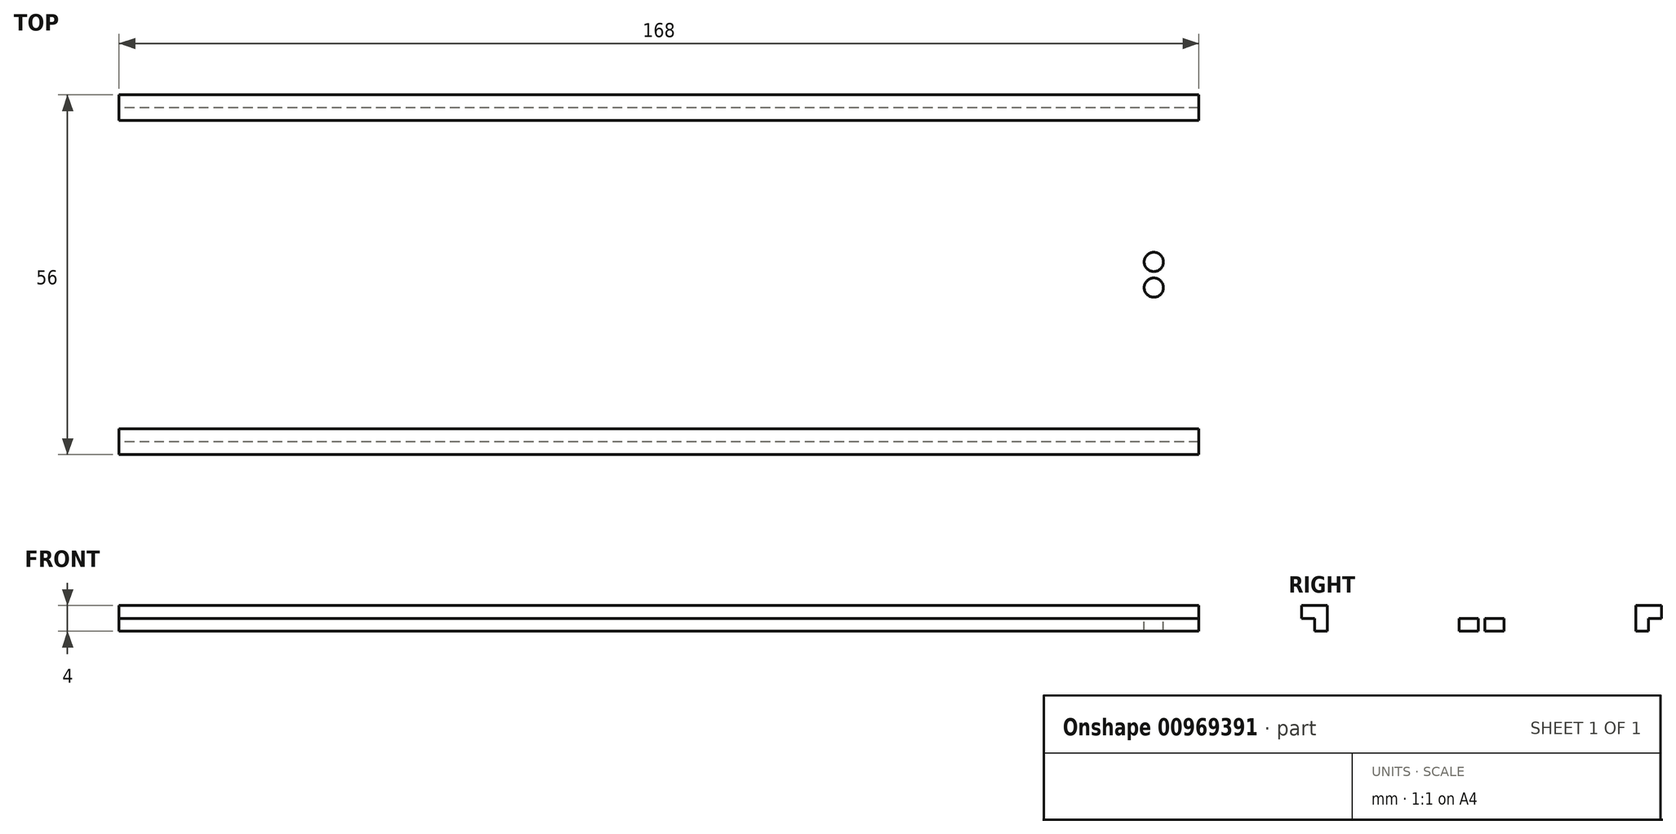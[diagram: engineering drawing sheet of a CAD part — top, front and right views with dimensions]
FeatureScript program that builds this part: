
annotation { "Feature Type Name" : "Feature", "Feature Type Description" : "" }
export const myFeature = defineFeature(function(context is Context, id is Id, definition is map)
    precondition{}
    {
        {
            var Q0;
            Q0=qCreatedBy(makeId("Top.planeOp"),FACE);
            var sketch = newSketch(context, id + "F0", { "sketchPlane" : qUnion([Q0])});
            skLineSegment(sketch, "E0.bottom", {"start": v(84, -26) * mm, "end": v(-84, -26) * mm});
            skLineSegment(sketch, "E0.top", {"start": v(84, 26) * mm, "end": v(-84, 26) * mm});
            skLineSegment(sketch, "E0.left", {"start": v(84, -26) * mm, "end": v(84, 26) * mm});
            skLineSegment(sketch, "E0.right", {"start": v(-84, -26) * mm, "end": v(-84, 26) * mm});
            skPoint(sketch, "E0.middle", {"position": v(0, 0) * mm});
            skSolve(sketch);
        }
        {
            var Q0;
            Q0=makeQuery(id+"F0.imprint","IMPRINT",FACE,{"disambiguationData":[TD([[makeQuery(id+"F0.imprint","IMPRINT",EDGE,{"derivedFrom":sQuery(id+"F0.wireOp",EDGE,"E0.bottom")}),-1.0]])]});
            extrude(context, id + "F1", {"entities" : qUnion([Q0]), "depth" : 2 * mm, "offsetDistance" : 25 * mm});
        }
        {
            var Q0;
            Q0=makeQuery(id+"F1.opExtrude","CAP_FACE",FACE,{"disambiguationData":[OSD([sQuery(id+"F0.wireOp",EDGE,"E0.bottom"),sQuery(id+"F0.wireOp",EDGE,"E0.top"),sQuery(id+"F0.wireOp",EDGE,"E0.left"),sQuery(id+"F0.wireOp",EDGE,"E0.right")])],"isStart":false});
            var sketch = newSketch(context, id + "F2", { "sketchPlane" : qUnion([Q0])});
            skLineSegment(sketch, "E1.bottom", {"start": v(-84, -24) * mm, "end": v(84, -24) * mm});
            skLineSegment(sketch, "E1.top", {"start": v(-84, -28) * mm, "end": v(84, -28) * mm});
            skLineSegment(sketch, "E1.left", {"start": v(-84, -24) * mm, "end": v(-84, -28) * mm});
            skLineSegment(sketch, "E1.right", {"start": v(84, -24) * mm, "end": v(84, -28) * mm});
            skLineSegment(sketch, "E2.bottom", {"start": v(-84, 24) * mm, "end": v(84, 24) * mm});
            skLineSegment(sketch, "E2.top", {"start": v(-84, 28) * mm, "end": v(84, 28) * mm});
            skLineSegment(sketch, "E2.left", {"start": v(-84, 24) * mm, "end": v(-84, 28) * mm});
            skLineSegment(sketch, "E2.right", {"start": v(84, 24) * mm, "end": v(84, 28) * mm});
            skSolve(sketch);
        }
        {
            var Q0;
            {var subQ0=sQuery(id+"F2.wireOp",EDGE,"E1.top");Q0=makeQuery(id+"F2.imprint","IMPRINT",FACE,{"disambiguationData":[TD([[makeQuery(id+"F2.imprint","IMPRINT",EDGE,{"derivedFrom":subQ0}),1.0]])]});}
            var Q1;
            {var subQ0=sQuery(id+"F2.wireOp",EDGE,"E1.bottom");Q1=makeQuery(id+"F2.imprint","IMPRINT",FACE,{"disambiguationData":[TD([[makeQuery(id+"F2.imprint","IMPRINT",EDGE,{"derivedFrom":subQ0}),-1.0]])]});}
            var Q2;
            {var subQ0=sQuery(id+"F2.wireOp",EDGE,"E2.bottom");Q2=makeQuery(id+"F2.imprint","IMPRINT",FACE,{"disambiguationData":[TD([[makeQuery(id+"F2.imprint","IMPRINT",EDGE,{"derivedFrom":subQ0}),1.0]])]});}
            var Q3;
            {var subQ0=sQuery(id+"F2.wireOp",EDGE,"E2.top");Q3=makeQuery(id+"F2.imprint","IMPRINT",FACE,{"disambiguationData":[TD([[makeQuery(id+"F2.imprint","IMPRINT",EDGE,{"derivedFrom":subQ0}),-1.0]])]});}
            extrude(context, id + "F3", {"entities" : qUnion([Q0, Q1, Q2, Q3]), "operationType" : NewBodyOperationType.ADD, "depth" : 2 * mm, "offsetDistance" : 25 * mm});
        }
        {
            var Q0;
            Q0=makeQuery(id+"F1.opExtrude","CAP_FACE",FACE,{"disambiguationData":[OSD([sQuery(id+"F0.wireOp",EDGE,"E0.bottom"),sQuery(id+"F0.wireOp",EDGE,"E0.top"),sQuery(id+"F0.wireOp",EDGE,"E0.left"),sQuery(id+"F0.wireOp",EDGE,"E0.right")])],"isStart":false});
            var sketch = newSketch(context, id + "F4", { "sketchPlane" : qUnion([Q0])});
            skLineSegment(sketch, "E3", {"start": v(-84, 0) * mm, "end": v(84, 0) * mm, "construction": true});
            skPoint(sketch, "E4", {"position": v(-77, 0) * mm});
            skLineSegment(sketch, "E5", {"start": v(-77, 0) * mm, "end": v(-77, 2) * mm, "construction": true});
            skLineSegment(sketch, "E6", {"start": v(-77, 0) * mm, "end": v(-77, -2) * mm, "construction": true});
            skCircle(sketch, "E7", {"center": v(-77, -2) * mm, "radius": 1.5 * mm});
            skCircle(sketch, "E8", {"center": v(-77, 2) * mm, "radius": 1.5 * mm});
            skLineSegment(sketch, "E9", {"start": v(-76, 0.88) * mm, "end": v(-76, -0.88) * mm});
            skLineSegment(sketch, "E10", {"start": v(-78, 0.88) * mm, "end": v(-78, -0.88) * mm});
            skLineSegment(sketch, "E11", {"start": v(0, 24) * mm, "end": v(0, -24) * mm, "construction": true});
            skLineSegment(sketch, "E12.MirrorCS", {"start": v(77, 0) * mm, "end": v(77, -2) * mm, "construction": true});
            skPoint(sketch, "E13.MirrorP", {"position": v(77, 0) * mm});
            skLineSegment(sketch, "E14.MirrorCS", {"start": v(78, 0.88) * mm, "end": v(78, -0.88) * mm});
            skLineSegment(sketch, "E15.MirrorCS", {"start": v(84, 0) * mm, "end": v(-84, 0) * mm, "construction": true});
            skLineSegment(sketch, "E16.MirrorCS", {"start": v(77, 0) * mm, "end": v(77, 2) * mm, "construction": true});
            skLineSegment(sketch, "E17.MirrorCS", {"start": v(76, 0.88) * mm, "end": v(76, -0.88) * mm});
            skCircle(sketch, "E18.MirrorC", {"center": v(77, -2) * mm, "radius": 1.5 * mm});
            skCircle(sketch, "E19.MirrorC", {"center": v(77, 2) * mm, "radius": 1.5 * mm});
            skSolve(sketch);
        }
        {
            var Q0;
            {var subQ0=sQuery(id+"F4.wireOp",EDGE,"E18.MirrorC");var subQ1=makeQuery(id+"F4.imprint","INTERSECT",VERTEX,{"derivedFrom":[sQuery(id+"F4.wireOp",EDGE,"E14.MirrorCS"),subQ0]});Q0=makeQuery(id+"F4.imprint","IMPRINT",FACE,{"disambiguationData":[TD([[makeQuery(id+"F4.imprint","IMPRINT",EDGE,{"disambiguationData":[TD([[subQ1,1.0]])],"derivedFrom":subQ0}),-1.0]])]});}
            var Q1;
            {var subQ0=sQuery(id+"F4.wireOp",EDGE,"E14.MirrorCS");Q1=makeQuery(id+"F4.imprint","IMPRINT",FACE,{"disambiguationData":[TD([[makeQuery(id+"F4.imprint","IMPRINT",EDGE,{"derivedFrom":subQ0}),-1.0]])]});}
            var Q2;
            {var subQ0=sQuery(id+"F4.wireOp",EDGE,"E19.MirrorC");var subQ1=makeQuery(id+"F4.imprint","INTERSECT",VERTEX,{"derivedFrom":[sQuery(id+"F4.wireOp",EDGE,"E14.MirrorCS"),subQ0]});Q2=makeQuery(id+"F4.imprint","IMPRINT",FACE,{"disambiguationData":[TD([[makeQuery(id+"F4.imprint","IMPRINT",EDGE,{"disambiguationData":[TD([[subQ1,-1.0]])],"derivedFrom":subQ0}),-1.0]])]});}
            var Q3;
            {var subQ0=sQuery(id+"F4.wireOp",EDGE,"E7");var subQ1=makeQuery(id+"F4.imprint","INTERSECT",VERTEX,{"derivedFrom":[subQ0,sQuery(id+"F4.wireOp",EDGE,"E9")]});Q3=makeQuery(id+"F4.imprint","IMPRINT",FACE,{"disambiguationData":[TD([[makeQuery(id+"F4.imprint","IMPRINT",EDGE,{"disambiguationData":[TD([[subQ1,-1.0]])],"derivedFrom":subQ0}),1.0]])]});}
            var Q4;
            {var subQ0=sQuery(id+"F4.wireOp",EDGE,"E9");Q4=makeQuery(id+"F4.imprint","IMPRINT",FACE,{"disambiguationData":[TD([[makeQuery(id+"F4.imprint","IMPRINT",EDGE,{"derivedFrom":subQ0}),-1.0]])]});}
            var Q5;
            {var subQ0=sQuery(id+"F4.wireOp",EDGE,"E8");var subQ1=makeQuery(id+"F4.imprint","INTERSECT",VERTEX,{"derivedFrom":[subQ0,sQuery(id+"F4.wireOp",EDGE,"E9")]});Q5=makeQuery(id+"F4.imprint","IMPRINT",FACE,{"disambiguationData":[TD([[makeQuery(id+"F4.imprint","IMPRINT",EDGE,{"disambiguationData":[TD([[subQ1,1.0]])],"derivedFrom":subQ0}),1.0]])]});}
            extrude(context, id + "F5", {"entities" : qUnion([Q0, Q1, Q2, Q3, Q4, Q5]), "operationType" : NewBodyOperationType.REMOVE, "oppositeDirection" : true, "depth" : 25 * mm, "offsetDistance" : 25 * mm});
        }
        {
            var Q0;
            Q0=makeQuery(id+"F1.opExtrude","CAP_FACE",FACE,{"disambiguationData":[OSD([sQuery(id+"F0.wireOp",EDGE,"E0.bottom"),sQuery(id+"F0.wireOp",EDGE,"E0.top"),sQuery(id+"F0.wireOp",EDGE,"E0.left"),sQuery(id+"F0.wireOp",EDGE,"E0.right")])],"isStart":false});
            var sketch = newSketch(context, id + "F6", { "sketchPlane" : qUnion([Q0])});
            skLineSegment(sketch, "E20.bottom", {"start": v(-84, 20) * mm, "end": v(-81.4, 20) * mm});
            skLineSegment(sketch, "E20.top", {"start": v(-84, 11.5) * mm, "end": v(-81.4, 11.5) * mm});
            skLineSegment(sketch, "E20.left", {"start": v(-84, 20) * mm, "end": v(-84, 11.5) * mm});
            skLineSegment(sketch, "E20.right", {"start": v(-81.4, 20) * mm, "end": v(-81.4, 11.5) * mm});
            skSolve(sketch);
        }
        {
            var Q0;
            Q0=makeQuery(id+"F6.imprint","IMPRINT",FACE,{"disambiguationData":[TD([[makeQuery(id+"F6.imprint","IMPRINT",EDGE,{"derivedFrom":sQuery(id+"F6.wireOp",EDGE,"E20.bottom")}),-1.0]])]});
            extrude(context, id + "F7", {"entities" : qUnion([Q0]), "operationType" : NewBodyOperationType.REMOVE, "oppositeDirection" : true, "depth" : 25 * mm, "offsetDistance" : 25 * mm});
        }
    });
